# Revit family: SSC_Straight Rail
name_source: partatom
category: Generic Models
revit_build: Autodesk Revit Architecture 2013 (Build: 20130531_2115(x64)
units: mm (PartAtom-declared; Revit-internal decimal feet)

## types (2) — shared parameters
Manufacturer = SURE CARE
URL = http://www.surecare.com.au

## per-type parameters (varying)
| type | Description | Length | Model | Rail Center Height | Rail Radius | Wall-Rail Center Offset |
| 300 x 32mm (SSC3032) | 300mm long x 32mm diameter straight rail concealed fixing | 300 mm | SSC3032 | 784 mm  [stored 2.57218 ft] | 16 mm  [stored 0.0524934 ft] | 71 mm  [stored 0.23294 ft] |
| 250 x 19mm (SSC2519) | 250mm long x 19mm diameter straight rail concealed fixing | 250 mm  [stored 0.82021 ft] | SSC2519 | 800 mm  [stored 2.62467 ft] | 9.5 mm | 64.5 mm  [stored 0.211614 ft] |

note: [stored X ft] marks values corroborated as IEEE doubles in the binary element streams (Revit-internal decimal feet)

## geometry (parser evidence)
native form markers: Sweep x2
no freeform markers — native parametric forms only
